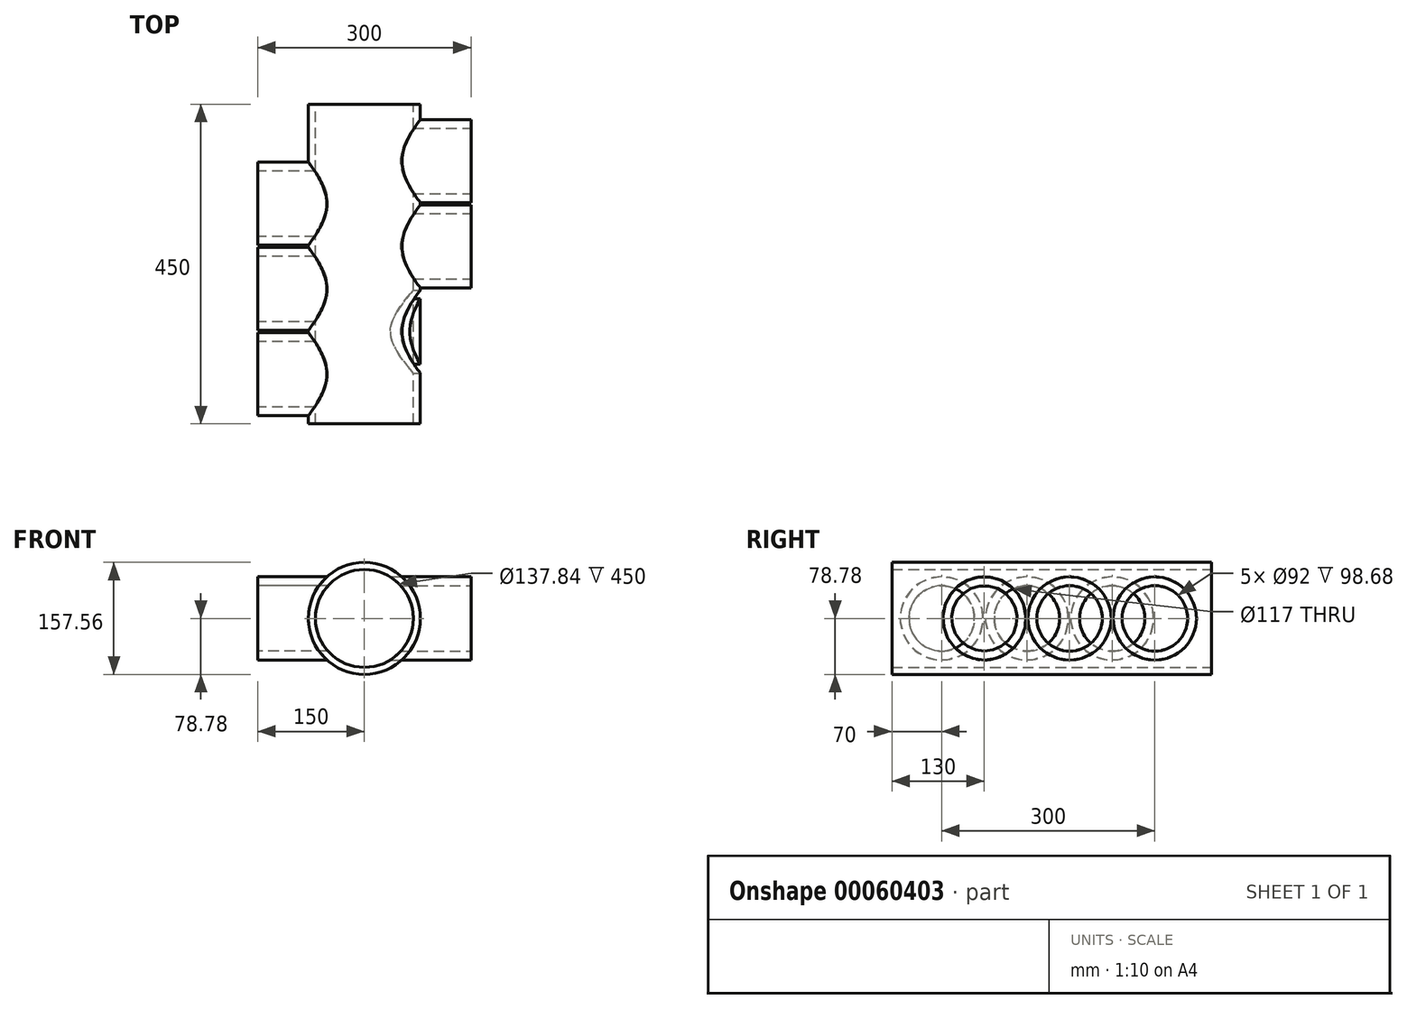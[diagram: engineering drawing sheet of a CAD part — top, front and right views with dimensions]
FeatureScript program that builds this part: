
annotation { "Feature Type Name" : "Feature", "Feature Type Description" : "" }
export const myFeature = defineFeature(function(context is Context, id is Id, definition is map)
    precondition{}
    {
        {
            var Q0;
            Q0=qCreatedBy(makeId("Right.planeOp"),FACE);
            cPlane(context, id + "F0", {"entities" : qUnion([Q0]), "cplaneType" : CPlaneType.OFFSET, "offset" : 150 * mm, "oppositeDirection" : true, "width" : 150 * mm, "height" : 150 * mm});
        }
        {
            var Q0;
            Q0=qCreatedBy(makeId("Right.planeOp"),FACE);
            cPlane(context, id + "F1", {"entities" : qUnion([Q0]), "cplaneType" : CPlaneType.OFFSET, "offset" : 150 * mm, "width" : 150 * mm, "height" : 150 * mm});
        }
        {
            var Q0;
            Q0=qCreatedBy(id+"F1.planeOp",FACE);
            var sketch = newSketch(context, id + "F2", { "sketchPlane" : qUnion([Q0])});
            skCircle(sketch, "E0", {"center": v(0, 0) * mm, "radius": 46 * mm});
            skCircle(sketch, "E1", {"center": v(120, 0) * mm, "radius": 46 * mm});
            skCircle(sketch, "E2", {"center": v(0, 0) * mm, "radius": 58.5 * mm});
            skCircle(sketch, "E3", {"center": v(120, 0) * mm, "radius": 58.5 * mm});
            skCircle(sketch, "E4.MirrorC", {"center": v(-120, 0) * mm, "radius": 46 * mm});
            skCircle(sketch, "E5.MirrorC", {"center": v(-120, 0) * mm, "radius": 58.5 * mm});
            skSolve(sketch);
        }
        {
            var Q0;
            Q0=qCreatedBy(id+"F0.planeOp",FACE);
            var sketch = newSketch(context, id + "F3", { "sketchPlane" : qUnion([Q0])});
            skCircle(sketch, "E6", {"center": v(60, 0) * mm, "radius": 58.5 * mm});
            skCircle(sketch, "E7", {"center": v(60, 0) * mm, "radius": 46 * mm});
            skCircle(sketch, "E8", {"center": v(-60, 0) * mm, "radius": 58.5 * mm});
            skCircle(sketch, "E9", {"center": v(-60, 0) * mm, "radius": 46 * mm});
            skCircle(sketch, "E10", {"center": v(-180, 0) * mm, "radius": 58.5 * mm});
            skCircle(sketch, "E11", {"center": v(-180, 0) * mm, "radius": 46 * mm});
            skSolve(sketch);
        }
        {
            var Q0;
            Q0=qCreatedBy(makeId("Front.planeOp"),FACE);
            var sketch = newSketch(context, id + "F4", { "sketchPlane" : qUnion([Q0])});
            skCircle(sketch, "E12", {"center": v(0, 0) * mm, "radius": 68.92 * mm});
            skCircle(sketch, "E13", {"center": v(0, 0) * mm, "radius": 78.78 * mm});
            skSolve(sketch);
        }
        {
            var Q0;
            Q0 = qSketchRegion(id + "F2", true);
            extrude(context, id + "F5", {"entities" : qUnion([Q0]), "oppositeDirection" : true, "depth" : 100 * mm});
        }
        {
            var Q0;
            Q0 = qSketchRegion(id + "F3", true);
            extrude(context, id + "F6", {"entities" : qUnion([Q0]), "depth" : 100 * mm});
        }
        {
            var Q0;
            Q0 = qSketchRegion(id + "F4", true);
            var Q1;
            Q1=makeQuery(id+"F6.opExtrude","SWEPT_BODY",BODY,{"disambiguationData":[OSD([sQuery(id+"F3.wireOp",EDGE,"E10"),sQuery(id+"F3.wireOp",EDGE,"E11")])]});
            extrude(context, id + "F7", {"entities" : qUnion([Q0]), "operationType" : NewBodyOperationType.ADD, "endBoundEntityBody" : qUnion([Q1]), "depth" : 250 * mm, "hasSecondDirection" : true, "secondDirectionOppositeDirection" : true, "secondDirectionDepth" : 200 * mm});
        }
        {
            var Q0;
            Q0=makeQuery(id+"F4.imprint","IMPRINT",FACE,{"disambiguationData":[TD([[makeQuery(id+"F4.imprint","IMPRINT",EDGE,{"derivedFrom":sQuery(id+"F4.wireOp",EDGE,"E12")}),1.0]])]});
            var Q1;
            Q1=sQuery(id+"F4.wireOp",EDGE,"E12");
            extrude(context, id + "F8", {"entities" : qUnion([Q0]), "operationType" : NewBodyOperationType.REMOVE, "surfaceEntities" : qUnion([Q1]), "endBound" : BoundingType.THROUGH_ALL, "oppositeDirection" : true, "depth" : 25 * mm, "hasSecondDirection" : true, "secondDirectionBound" : SecondDirectionBoundingType.THROUGH_ALL, "secondDirectionOppositeDirection" : false, "secondDirectionDepth" : 25 * mm});
        }
        {
            var Q0;
            Q0=makeQuery(id+"F2.imprint","IMPRINT",FACE,{"disambiguationData":[TD([[makeQuery(id+"F2.imprint","IMPRINT",EDGE,{"derivedFrom":sQuery(id+"F2.wireOp",EDGE,"E1")}),1.0]])]});
            var Q1;
            Q1=makeQuery(id+"F2.imprint","IMPRINT",FACE,{"disambiguationData":[TD([[makeQuery(id+"F2.imprint","IMPRINT",EDGE,{"derivedFrom":sQuery(id+"F2.wireOp",EDGE,"E0")}),1.0]])]});
            var Q2;
            Q2=makeQuery(id+"F2.imprint","IMPRINT",FACE,{"disambiguationData":[TD([[makeQuery(id+"F2.imprint","IMPRINT",EDGE,{"derivedFrom":sQuery(id+"F2.wireOp",EDGE,"E4.MirrorC")}),-1.0]])]});
            var Q3;
            Q3=qCreatedBy(makeId("Right.planeOp"),FACE);
            extrude(context, id + "F9", {"entities" : qUnion([Q0, Q1, Q2]), "operationType" : NewBodyOperationType.REMOVE, "endBound" : BoundingType.UP_TO_SURFACE, "oppositeDirection" : true, "endBoundEntityFace" : qUnion([Q3]), "depth" : 25 * mm});
        }
        {
            var Q0;
            Q0=makeQuery(id+"F3.imprint","IMPRINT",FACE,{"disambiguationData":[TD([[makeQuery(id+"F3.imprint","IMPRINT",EDGE,{"derivedFrom":sQuery(id+"F3.wireOp",EDGE,"E7")}),1.0]])]});
            var Q1;
            Q1=makeQuery(id+"F3.imprint","IMPRINT",FACE,{"disambiguationData":[TD([[makeQuery(id+"F3.imprint","IMPRINT",EDGE,{"derivedFrom":sQuery(id+"F3.wireOp",EDGE,"E9")}),1.0]])]});
            var Q2;
            Q2=makeQuery(id+"F3.imprint","IMPRINT",FACE,{"disambiguationData":[TD([[makeQuery(id+"F3.imprint","IMPRINT",EDGE,{"derivedFrom":sQuery(id+"F3.wireOp",EDGE,"E11")}),1.0]])]});
            var Q3;
            Q3=qCreatedBy(makeId("Right.planeOp"),FACE);
            extrude(context, id + "F10", {"entities" : qUnion([Q0, Q1, Q2]), "operationType" : NewBodyOperationType.REMOVE, "endBound" : BoundingType.UP_TO_SURFACE, "endBoundEntityFace" : qUnion([Q3]), "depth" : 25 * mm});
        }
    });
